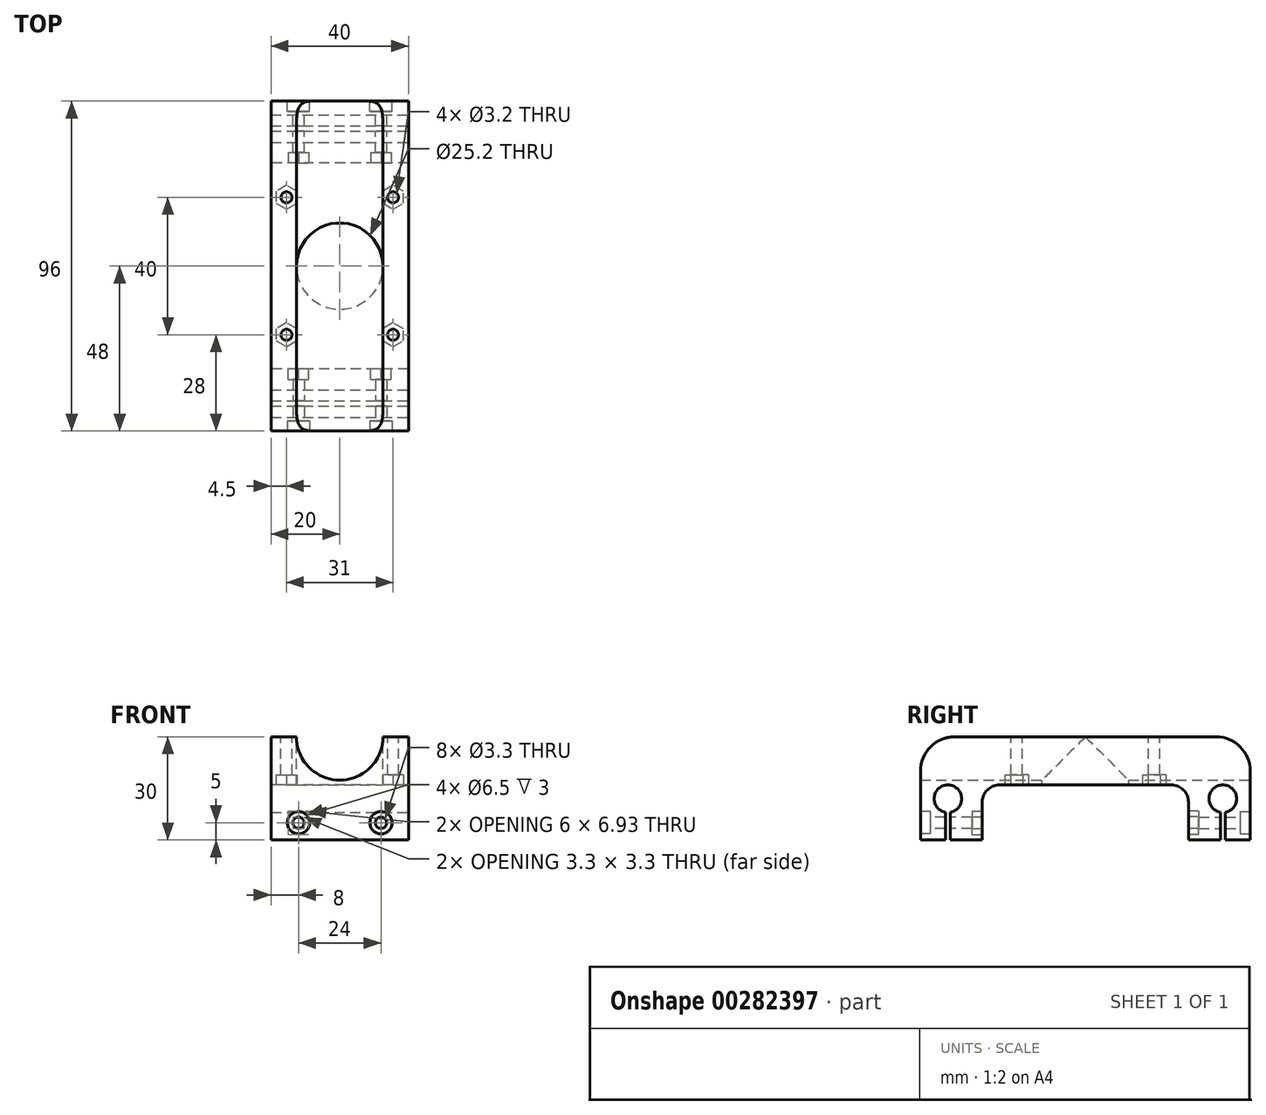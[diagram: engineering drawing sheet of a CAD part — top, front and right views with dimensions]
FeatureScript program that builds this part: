
annotation { "Feature Type Name" : "Feature", "Feature Type Description" : "" }
export const myFeature = defineFeature(function(context is Context, id is Id, definition is map)
    precondition{}
    {
        {
            var Q0;
            Q0=qCreatedBy(makeId("Front.planeOp"),FACE);
            var sketch = newSketch(context, id + "F0", { "sketchPlane" : qUnion([Q0])});
            skLineSegment(sketch, "E0.bottom", {"start": v(0, 0) * mm, "end": v(40, 0) * mm});
            skLineSegment(sketch, "E0.top", {"start": v(0, 30) * mm, "end": v(7.4, 30) * mm});
            skLineSegment(sketch, "E0.left", {"start": v(0, 0) * mm, "end": v(0, 30) * mm});
            skLineSegment(sketch, "E0.right", {"start": v(40, 0) * mm, "end": v(40, 30) * mm});
            skArc(sketch, "E1", {"start": v(7.4, 30) * mm, "mid": v(20, 17.4) * mm, "end": v(32.6, 30) * mm});
            skLineSegment(sketch, "E2.trimOffspring", {"start": v(32.6, 30) * mm, "end": v(40, 30) * mm});
            skSolve(sketch);
        }
        {
            var Q0;
            Q0=qSketchRegion(id+"F0",true);
            extrude(context, id + "F1", {"entities" : qUnion([Q0]), "depth" : 96 * mm});
        }
        {
            var Q0;
            Q0=makeQuery(id+"F1.opExtrude","SWEPT_FACE",FACE,{"disambiguationData":[OSD([sQuery(id+"F0.wireOp",EDGE,"E0.right")])]});
            var sketch = newSketch(context, id + "F2", { "sketchPlane" : qUnion([Q0])});
            skLineSegment(sketch, "E3", {"start": v(-88, 30) * mm, "end": v(-88, 0) * mm, "construction": true});
            skLineSegment(sketch, "E4", {"start": v(-8, 30) * mm, "end": v(-8, 0) * mm, "construction": true});
            skArc(sketch, "E5", {"start": v(-87.25, 8.07) * mm, "mid": v(-88, 16) * mm, "end": v(-88.75, 8.07) * mm});
            skArc(sketch, "E6", {"start": v(-7.25, 8.07) * mm, "mid": v(-8, 16) * mm, "end": v(-8.75, 8.07) * mm});
            skLineSegment(sketch, "E7.0", {"start": v(-87.25, 8.07) * mm, "end": v(-87.25, 0) * mm});
            skLineSegment(sketch, "E8.0", {"start": v(-88.75, 8.07) * mm, "end": v(-88.75, 0) * mm});
            skLineSegment(sketch, "E9.0", {"start": v(-8.75, 8.07) * mm, "end": v(-8.75, 0) * mm});
            skLineSegment(sketch, "E10.0", {"start": v(-7.25, 8.07) * mm, "end": v(-7.25, 0) * mm});
            skLineSegment(sketch, "E11", {"start": v(-8.75, 0) * mm, "end": v(-7.25, 0) * mm});
            skLineSegment(sketch, "E12", {"start": v(-88.75, 0) * mm, "end": v(-87.25, 0) * mm});
            skSolve(sketch);
        }
        {
            var Q0;
            Q0=qSketchRegion(id+"F2",true);
            extrude(context, id + "F3", {"entities" : qUnion([Q0]), "operationType" : NewBodyOperationType.REMOVE, "endBound" : BoundingType.THROUGH_ALL, "oppositeDirection" : true, "depth" : 25 * mm});
        }
        {
            var Q0;
            Q0=makeQuery(id+"F1.opExtrude","CAP_FACE",FACE,{"disambiguationData":[OSD([sQuery(id+"F0.wireOp",EDGE,"E0.bottom"),sQuery(id+"F0.wireOp",EDGE,"E0.top"),sQuery(id+"F0.wireOp",EDGE,"E0.left"),sQuery(id+"F0.wireOp",EDGE,"E0.right"),sQuery(id+"F0.wireOp",EDGE,"E1"),sQuery(id+"F0.wireOp",EDGE,"E2.trimOffspring")])],"isStart":true});
            var sketch = newSketch(context, id + "F4", { "sketchPlane" : qUnion([Q0])});
            skLineSegment(sketch, "E13", {"start": v(-40, 5) * mm, "end": v(0, 5) * mm, "construction": true});
            skLineSegment(sketch, "E14", {"start": v(-20, 0) * mm, "end": v(-20, 17.4) * mm, "construction": true});
            skPoint(sketch, "E15", {"position": v(-32, 5) * mm});
            skPoint(sketch, "E16", {"position": v(-8, 5) * mm});
            skSolve(sketch);
        }
        {
            var Q0;
            Q0=makeQuery(id+"F1.opExtrude","CAP_FACE",FACE,{"disambiguationData":[OSD([sQuery(id+"F0.wireOp",EDGE,"E0.bottom"),sQuery(id+"F0.wireOp",EDGE,"E0.top"),sQuery(id+"F0.wireOp",EDGE,"E0.left"),sQuery(id+"F0.wireOp",EDGE,"E0.right"),sQuery(id+"F0.wireOp",EDGE,"E1"),sQuery(id+"F0.wireOp",EDGE,"E2.trimOffspring")])],"isStart":false});
            var sketch = newSketch(context, id + "F5", { "sketchPlane" : qUnion([Q0])});
            skLineSegment(sketch, "E17", {"start": v(0, 5) * mm, "end": v(40, 5) * mm, "construction": true});
            skLineSegment(sketch, "E18", {"start": v(20, 0) * mm, "end": v(20, 17.4) * mm, "construction": true});
            skPoint(sketch, "E19", {"position": v(8, 5) * mm});
            skPoint(sketch, "E20", {"position": v(32, 5) * mm});
            skSolve(sketch);
        }
        {
            var Q0;
            Q0=sQuery(id+"F5.wireOp",VERTEX,"E19");
            var Q1;
            Q1=sQuery(id+"F5.wireOp",VERTEX,"E20");
            var Q2;
            Q2=sQuery(id+"F4.wireOp",VERTEX,"E16");
            var Q3;
            Q3=sQuery(id+"F4.wireOp",VERTEX,"E15");
            var Q4;
            Q4=makeQuery(id+"F1.opExtrude","SWEPT_BODY",BODY,{"disambiguationData":[OSD([sQuery(id+"F0.wireOp",EDGE,"E0.bottom"),sQuery(id+"F0.wireOp",EDGE,"E0.top"),sQuery(id+"F0.wireOp",EDGE,"E0.left"),sQuery(id+"F0.wireOp",EDGE,"E0.right"),sQuery(id+"F0.wireOp",EDGE,"E1"),sQuery(id+"F0.wireOp",EDGE,"E2.trimOffspring")])]});
            hole(context, id + "F6", {"style" : HoleStyle.C_BORE, "endStyle" : HoleEndStyle.BLIND, "standardTappedOrClearance" : lookupTablePath({ "standard" : "ISO", "fit" : "Normal", "size" : "M3", "type" : "Clearance" }), "standardBlindInLast" : lookupTablePath({ "fit" : "Standard", "standard" : "ISO", "size" : "M3", "type" : "Clearance" }), "holeDiameter" : 3.3 * mm, "cBoreDiameter" : 6.5 * mm, "cBoreDepth" : 3 * mm, "holeDepth" : 30 * mm, "tappedDepth" : 3 * mm, "tapClearance" : 3, "startFromSketch" : true, "locations" : qUnion([Q0, Q1, Q2, Q3]), "scope" : qUnion([Q4])});
        }
        {
            var Q0;
            Q0=makeQuery(id+"F1.opExtrude","SWEPT_FACE",FACE,{"disambiguationData":[OSD([sQuery(id+"F0.wireOp",EDGE,"E0.left")])]});
            var sketch = newSketch(context, id + "F7", { "sketchPlane" : qUnion([Q0])});
            skLineSegment(sketch, "E21.bottom", {"start": v(18, 0) * mm, "end": v(78, 0) * mm});
            skLineSegment(sketch, "E21.top", {"start": v(23, 16) * mm, "end": v(73, 16) * mm});
            skLineSegment(sketch, "E21.left", {"start": v(18, 0) * mm, "end": v(18, 11) * mm});
            skLineSegment(sketch, "E21.right", {"start": v(78, 0) * mm, "end": v(78, 11) * mm});
            skPoint(sketch, "E22.visualSharp", {"position": v(18, 16) * mm});
            skArc(sketch, "E22.filletArc", {"start": v(23, 16) * mm, "mid": v(19.46, 14.54) * mm, "end": v(18, 11) * mm});
            skPoint(sketch, "E23.visualSharp", {"position": v(78, 16) * mm});
            skArc(sketch, "E23.filletArc", {"start": v(78, 11) * mm, "mid": v(76.54, 14.54) * mm, "end": v(73, 16) * mm});
            skSolve(sketch);
        }
        {
            var Q0;
            Q0=qSketchRegion(id+"F7",true);
            extrude(context, id + "F8", {"entities" : qUnion([Q0]), "operationType" : NewBodyOperationType.REMOVE, "endBound" : BoundingType.THROUGH_ALL, "oppositeDirection" : true, "depth" : 25 * mm});
        }
        {
            var Q0;
            Q0=makeQuery(id+"F8.boolean.opBoolean","COPY",FACE,{"derivedFrom":makeQuery(id+"F8.opExtrude","SWEPT_FACE",FACE,{"disambiguationData":[OSD([sQuery(id+"F7.wireOp",EDGE,"E21.top")])]})});
            var sketch = newSketch(context, id + "F9", { "sketchPlane" : qUnion([Q0])});
            skLineSegment(sketch, "E24", {"start": v(0, 48) * mm, "end": v(40, 48) * mm, "construction": true});
            skLineSegment(sketch, "E25", {"start": v(4.5, 73) * mm, "end": v(4.5, 23) * mm, "construction": true});
            skLineSegment(sketch, "E26", {"start": v(35.5, 73) * mm, "end": v(35.5, 23) * mm, "construction": true});
            skCircle(sketch, "E27.cCircle", {"center": v(4.5, 68) * mm, "radius": 3 * mm, "construction": true});
            skLineSegment(sketch, "E27.0", {"start": v(7.5, 69.73) * mm, "end": v(7.5, 66.27) * mm});
            skLineSegment(sketch, "E27.1", {"start": v(7.5, 66.27) * mm, "end": v(4.5, 64.54) * mm});
            skLineSegment(sketch, "E27.2", {"start": v(4.5, 64.54) * mm, "end": v(1.5, 66.27) * mm});
            skLineSegment(sketch, "E27.3", {"start": v(1.5, 66.27) * mm, "end": v(1.5, 69.73) * mm});
            skLineSegment(sketch, "E27.4", {"start": v(1.5, 69.73) * mm, "end": v(4.5, 71.46) * mm});
            skLineSegment(sketch, "E27.5", {"start": v(4.5, 71.46) * mm, "end": v(7.5, 69.73) * mm});
            skPoint(sketch, "E27.0.midPoint", {"position": v(7.5, 68) * mm});
            skCircle(sketch, "E28.cCircle", {"center": v(35.5, 68) * mm, "radius": 3 * mm, "construction": true});
            skLineSegment(sketch, "E28.0", {"start": v(32.5, 66.27) * mm, "end": v(32.5, 69.73) * mm});
            skLineSegment(sketch, "E28.1", {"start": v(32.5, 69.73) * mm, "end": v(35.5, 71.46) * mm});
            skLineSegment(sketch, "E28.2", {"start": v(35.5, 71.46) * mm, "end": v(38.5, 69.73) * mm});
            skLineSegment(sketch, "E28.3", {"start": v(38.5, 69.73) * mm, "end": v(38.5, 66.27) * mm});
            skLineSegment(sketch, "E28.4", {"start": v(38.5, 66.27) * mm, "end": v(35.5, 64.54) * mm});
            skLineSegment(sketch, "E28.5", {"start": v(35.5, 64.54) * mm, "end": v(32.5, 66.27) * mm});
            skPoint(sketch, "E28.0.midPoint", {"position": v(32.5, 68) * mm});
            skCircle(sketch, "E29.cCircle", {"center": v(4.5, 28) * mm, "radius": 3 * mm, "construction": true});
            skLineSegment(sketch, "E29.0", {"start": v(7.5, 29.73) * mm, "end": v(7.5, 26.27) * mm});
            skLineSegment(sketch, "E29.1", {"start": v(7.5, 26.27) * mm, "end": v(4.5, 24.54) * mm});
            skLineSegment(sketch, "E29.2", {"start": v(4.5, 24.54) * mm, "end": v(1.5, 26.27) * mm});
            skLineSegment(sketch, "E29.3", {"start": v(1.5, 26.27) * mm, "end": v(1.5, 29.73) * mm});
            skLineSegment(sketch, "E29.4", {"start": v(1.5, 29.73) * mm, "end": v(4.5, 31.46) * mm});
            skLineSegment(sketch, "E29.5", {"start": v(4.5, 31.46) * mm, "end": v(7.5, 29.73) * mm});
            skPoint(sketch, "E29.0.midPoint", {"position": v(7.5, 28) * mm});
            skCircle(sketch, "E30.cCircle", {"center": v(35.5, 28) * mm, "radius": 3 * mm, "construction": true});
            skLineSegment(sketch, "E30.0", {"start": v(32.5, 26.27) * mm, "end": v(32.5, 29.73) * mm});
            skLineSegment(sketch, "E30.1", {"start": v(32.5, 29.73) * mm, "end": v(35.5, 31.46) * mm});
            skLineSegment(sketch, "E30.2", {"start": v(35.5, 31.46) * mm, "end": v(38.5, 29.73) * mm});
            skLineSegment(sketch, "E30.3", {"start": v(38.5, 29.73) * mm, "end": v(38.5, 26.27) * mm});
            skLineSegment(sketch, "E30.4", {"start": v(38.5, 26.27) * mm, "end": v(35.5, 24.54) * mm});
            skLineSegment(sketch, "E30.5", {"start": v(35.5, 24.54) * mm, "end": v(32.5, 26.27) * mm});
            skPoint(sketch, "E30.0.midPoint", {"position": v(32.5, 28) * mm});
            skLineSegment(sketch, "E31", {"start": v(4.5, 28) * mm, "end": v(7.5, 28) * mm, "construction": true});
            skLineSegment(sketch, "E32", {"start": v(7.5, 68) * mm, "end": v(4.5, 68) * mm, "construction": true});
            skLineSegment(sketch, "E33", {"start": v(32.5, 28) * mm, "end": v(35.5, 28) * mm, "construction": true});
            skLineSegment(sketch, "E34", {"start": v(32.5, 68) * mm, "end": v(35.5, 68) * mm, "construction": true});
            skSolve(sketch);
        }
        {
            var Q0;
            Q0=qSketchRegion(id+"F9",true);
            extrude(context, id + "F10", {"entities" : qUnion([Q0]), "operationType" : NewBodyOperationType.REMOVE, "oppositeDirection" : true, "depth" : 3 * mm});
        }
        {
            var Q0;
            Q0=makeQuery(id+"F8.boolean.opBoolean","COPY",FACE,{"derivedFrom":makeQuery(id+"F8.opExtrude","SWEPT_FACE",FACE,{"disambiguationData":[OSD([sQuery(id+"F7.wireOp",EDGE,"E21.left")])]})});
            var sketch = newSketch(context, id + "F11", { "sketchPlane" : qUnion([Q0])});
            skCircle(sketch, "E35.cCircle", {"center": v(8, 5) * mm, "radius": 3 * mm, "construction": true});
            skLineSegment(sketch, "E35.0", {"start": v(11, 6.73) * mm, "end": v(11, 3.27) * mm});
            skLineSegment(sketch, "E35.1", {"start": v(11, 3.27) * mm, "end": v(8, 1.54) * mm});
            skLineSegment(sketch, "E35.2", {"start": v(8, 1.54) * mm, "end": v(5, 3.27) * mm});
            skLineSegment(sketch, "E35.3", {"start": v(5, 3.27) * mm, "end": v(5, 6.73) * mm});
            skLineSegment(sketch, "E35.4", {"start": v(5, 6.73) * mm, "end": v(8, 8.46) * mm});
            skLineSegment(sketch, "E35.5", {"start": v(8, 8.46) * mm, "end": v(11, 6.73) * mm});
            skPoint(sketch, "E35.0.midPoint", {"position": v(11, 5) * mm});
            skCircle(sketch, "E36.cCircle", {"center": v(32, 5) * mm, "radius": 3 * mm, "construction": true});
            skLineSegment(sketch, "E36.0", {"start": v(35, 6.73) * mm, "end": v(35, 3.27) * mm});
            skLineSegment(sketch, "E36.1", {"start": v(35, 3.27) * mm, "end": v(32, 1.54) * mm});
            skLineSegment(sketch, "E36.2", {"start": v(32, 1.54) * mm, "end": v(29, 3.27) * mm});
            skLineSegment(sketch, "E36.3", {"start": v(29, 3.27) * mm, "end": v(29, 6.73) * mm});
            skLineSegment(sketch, "E36.4", {"start": v(29, 6.73) * mm, "end": v(32, 8.46) * mm});
            skLineSegment(sketch, "E36.5", {"start": v(32, 8.46) * mm, "end": v(35, 6.73) * mm});
            skPoint(sketch, "E36.0.midPoint", {"position": v(35, 5) * mm});
            skLineSegment(sketch, "E37", {"start": v(32, 5) * mm, "end": v(35, 5) * mm, "construction": true});
            skLineSegment(sketch, "E38", {"start": v(8, 5) * mm, "end": v(11, 5) * mm, "construction": true});
            skSolve(sketch);
        }
        {
            var Q0;
            Q0=qSketchRegion(id+"F11",true);
            extrude(context, id + "F12", {"entities" : qUnion([Q0]), "operationType" : NewBodyOperationType.REMOVE, "oppositeDirection" : true, "depth" : 3 * mm});
        }
        {
            var Q0;
            Q0=makeQuery(id+"F8.boolean.opBoolean","COPY",FACE,{"derivedFrom":makeQuery(id+"F8.opExtrude","SWEPT_FACE",FACE,{"disambiguationData":[OSD([sQuery(id+"F7.wireOp",EDGE,"E21.right")])]})});
            var sketch = newSketch(context, id + "F13", { "sketchPlane" : qUnion([Q0])});
            skCircle(sketch, "E39.cCircle", {"center": v(-32, 5) * mm, "radius": 3 * mm, "construction": true});
            skLineSegment(sketch, "E39.0", {"start": v(-35, 3.27) * mm, "end": v(-35, 6.73) * mm});
            skLineSegment(sketch, "E39.1", {"start": v(-35, 6.73) * mm, "end": v(-32, 8.46) * mm});
            skLineSegment(sketch, "E39.2", {"start": v(-32, 8.46) * mm, "end": v(-29, 6.73) * mm});
            skLineSegment(sketch, "E39.3", {"start": v(-29, 6.73) * mm, "end": v(-29, 3.27) * mm});
            skLineSegment(sketch, "E39.4", {"start": v(-29, 3.27) * mm, "end": v(-32, 1.54) * mm});
            skLineSegment(sketch, "E39.5", {"start": v(-32, 1.54) * mm, "end": v(-35, 3.27) * mm});
            skPoint(sketch, "E39.0.midPoint", {"position": v(-35, 5) * mm});
            skCircle(sketch, "E40.cCircle", {"center": v(-8, 5) * mm, "radius": 3 * mm, "construction": true});
            skLineSegment(sketch, "E40.0", {"start": v(-11, 3.27) * mm, "end": v(-11, 6.73) * mm});
            skLineSegment(sketch, "E40.1", {"start": v(-11, 6.73) * mm, "end": v(-8, 8.46) * mm});
            skLineSegment(sketch, "E40.2", {"start": v(-8, 8.46) * mm, "end": v(-5, 6.73) * mm});
            skLineSegment(sketch, "E40.3", {"start": v(-5, 6.73) * mm, "end": v(-5, 3.27) * mm});
            skLineSegment(sketch, "E40.4", {"start": v(-5, 3.27) * mm, "end": v(-8, 1.54) * mm});
            skLineSegment(sketch, "E40.5", {"start": v(-8, 1.54) * mm, "end": v(-11, 3.27) * mm});
            skPoint(sketch, "E40.0.midPoint", {"position": v(-11, 5) * mm});
            skLineSegment(sketch, "E41", {"start": v(-11, 5) * mm, "end": v(-8, 5) * mm, "construction": true});
            skLineSegment(sketch, "E42", {"start": v(-35, 5) * mm, "end": v(-32, 5) * mm, "construction": true});
            skSolve(sketch);
        }
        {
            var Q0;
            Q0=qSketchRegion(id+"F13",true);
            extrude(context, id + "F14", {"entities" : qUnion([Q0]), "operationType" : NewBodyOperationType.REMOVE, "oppositeDirection" : true, "depth" : 3 * mm});
        }
        {
            var Q0;
            Q0=makeQuery(id+"F1.opExtrude","SWEPT_FACE",FACE,{"disambiguationData":[OSD([sQuery(id+"F0.wireOp",EDGE,"E0.top")])]});
            var sketch = newSketch(context, id + "F15", { "sketchPlane" : qUnion([Q0])});
            skLineSegment(sketch, "E43", {"start": v(0, -48) * mm, "end": v(40, -48) * mm, "construction": true});
            skLineSegment(sketch, "E44", {"start": v(4.5, 0) * mm, "end": v(4.5, -96) * mm, "construction": true});
            skLineSegment(sketch, "E45", {"start": v(4.5, -96) * mm, "end": v(35.5, -96) * mm, "construction": true});
            skLineSegment(sketch, "E46", {"start": v(35.5, -96) * mm, "end": v(35.5, 0) * mm, "construction": true});
            skLineSegment(sketch, "E47", {"start": v(35.5, 0) * mm, "end": v(4.5, 0) * mm, "construction": true});
            skCircle(sketch, "E48", {"center": v(4.5, -28) * mm, "radius": 1.6 * mm});
            skCircle(sketch, "E49", {"center": v(35.5, -28) * mm, "radius": 1.6 * mm});
            skCircle(sketch, "E50", {"center": v(35.5, -68) * mm, "radius": 1.6 * mm});
            skCircle(sketch, "E51", {"center": v(4.5, -68) * mm, "radius": 1.6 * mm});
            skCircle(sketch, "E52", {"center": v(20, -48) * mm, "radius": 12.6 * mm});
            skSolve(sketch);
        }
        {
            var Q0;
            Q0=qSketchRegion(id+"F15",true);
            extrude(context, id + "F16", {"entities" : qUnion([Q0]), "operationType" : NewBodyOperationType.REMOVE, "oppositeDirection" : true, "depth" : 25 * mm});
        }
        {
            var Q0;
            Q0=makeQuery(id+"F1.opExtrude","CAP_EDGE",EDGE,{"disambiguationData":[OSD([sQuery(id+"F0.wireOp",EDGE,"E2.trimOffspring")])],"isStart":false});
            var Q1;
            Q1=makeQuery(id+"F1.opExtrude","CAP_EDGE",EDGE,{"disambiguationData":[OSD([sQuery(id+"F0.wireOp",EDGE,"E0.top")])],"isStart":false});
            var Q2;
            Q2=makeQuery(id+"F1.opExtrude","CAP_EDGE",EDGE,{"disambiguationData":[OSD([sQuery(id+"F0.wireOp",EDGE,"E0.top")])],"isStart":true});
            var Q3;
            Q3=makeQuery(id+"F1.opExtrude","CAP_EDGE",EDGE,{"disambiguationData":[OSD([sQuery(id+"F0.wireOp",EDGE,"E2.trimOffspring")])],"isStart":true});
            fillet(context, id + "F17", {"entities" : qUnion([Q0, Q1, Q2, Q3]), "radius" : 10 * mm, "tangentPropagation" : true, "allowEdgeOverflow" : false});
        }
    });
